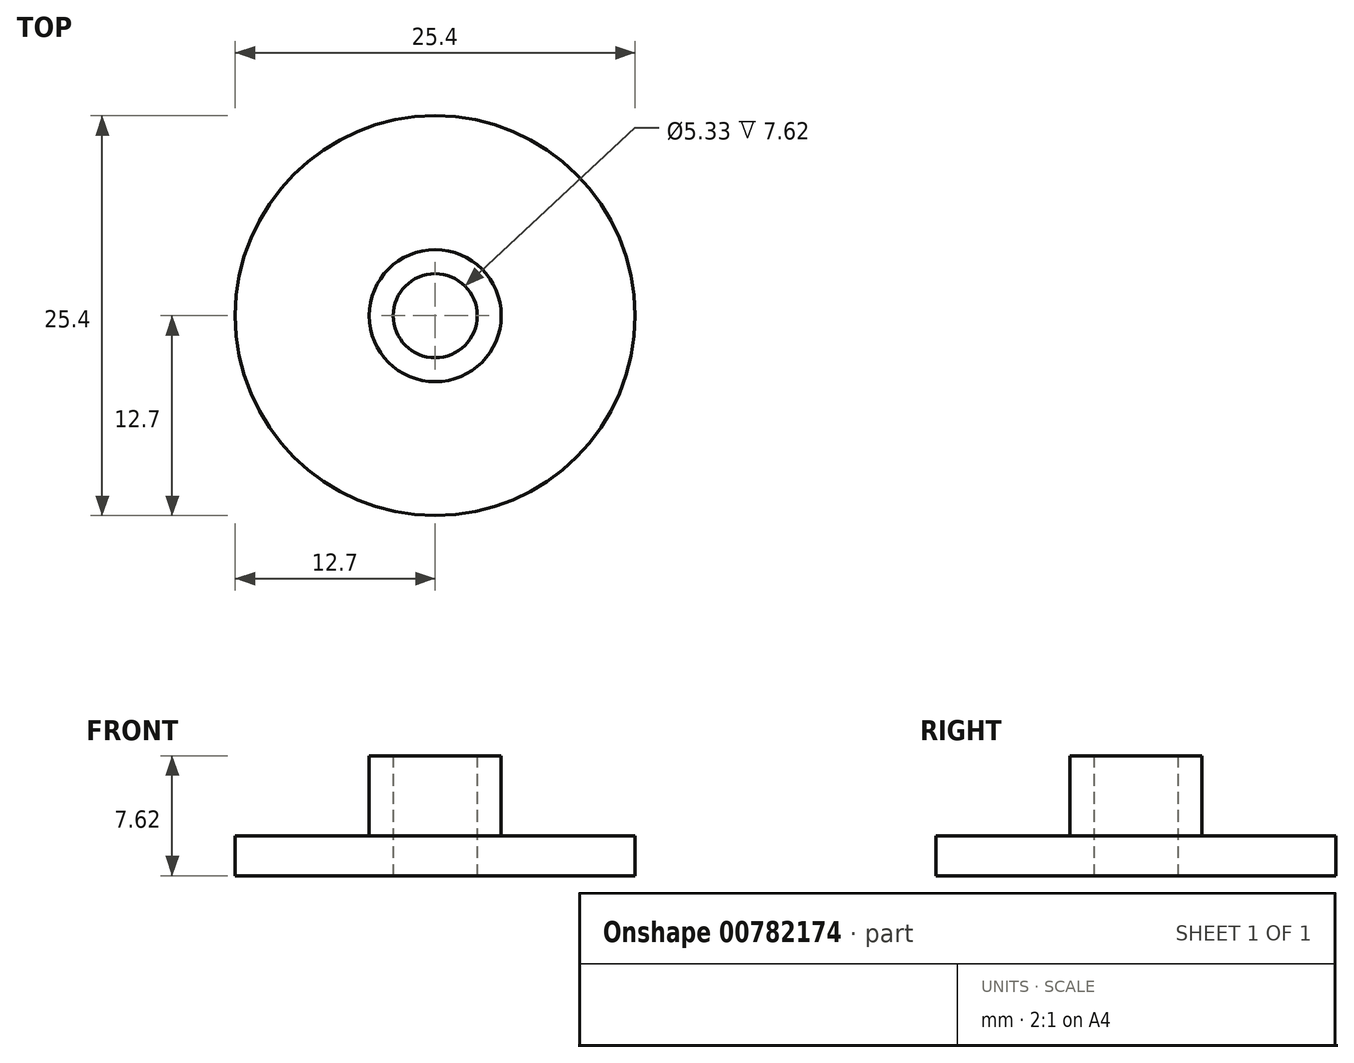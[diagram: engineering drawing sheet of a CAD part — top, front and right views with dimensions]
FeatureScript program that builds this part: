
annotation { "Feature Type Name" : "Feature", "Feature Type Description" : "" }
export const myFeature = defineFeature(function(context is Context, id is Id, definition is map)
    precondition{}
    {
        {
            var Q0;
            Q0=qCreatedBy(makeId("Top.planeOp"),FACE);
            var sketch = newSketch(context, id + "F0", { "sketchPlane" : qUnion([Q0])});
            skCircle(sketch, "E0", {"center": v(0, 0) * mm, "radius": 12.7 * mm});
            skSolve(sketch);
        }
        {
            var Q0;
            Q0 = qSketchRegion(id + "F0", true);
            extrude(context, id + "F1", {"entities" : qUnion([Q0]), "depth" : 2.54 * mm, "offsetDistance" : 25.4 * mm});
        }
        {
            var Q0;
            Q0=qCreatedBy(makeId("Top.planeOp"),FACE);
            var sketch = newSketch(context, id + "F2", { "sketchPlane" : qUnion([Q0])});
            skCircle(sketch, "E1", {"center": v(0, 0) * mm, "radius": 4.2 * mm});
            skSolve(sketch);
        }
        {
            var Q0;
            Q0 = qSketchRegion(id + "F2", true);
            extrude(context, id + "F3", {"entities" : qUnion([Q0]), "operationType" : NewBodyOperationType.ADD, "depth" : 7.62 * mm, "offsetDistance" : 25.4 * mm});
        }
        {
            var Q0;
            Q0=qCreatedBy(makeId("Top.planeOp"),FACE);
            var sketch = newSketch(context, id + "F4", { "sketchPlane" : qUnion([Q0])});
            skCircle(sketch, "E2", {"center": v(0, 0) * mm, "radius": 2.67 * mm});
            skSolve(sketch);
        }
        {
            var Q0;
            Q0 = qSketchRegion(id + "F4", true);
            extrude(context, id + "F5", {"entities" : qUnion([Q0]), "operationType" : NewBodyOperationType.REMOVE, "endBound" : BoundingType.THROUGH_ALL, "depth" : 25.4 * mm, "offsetDistance" : 25.4 * mm});
        }
    });
